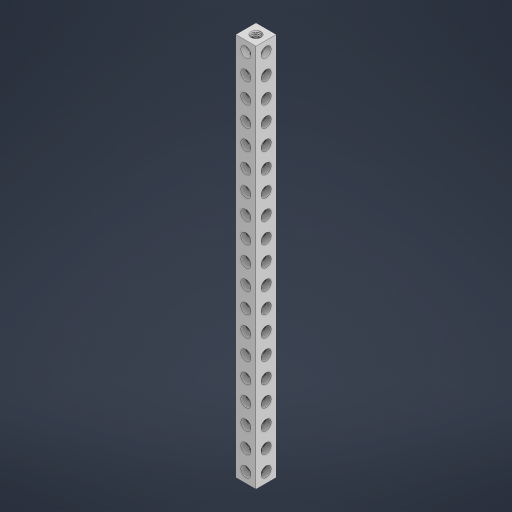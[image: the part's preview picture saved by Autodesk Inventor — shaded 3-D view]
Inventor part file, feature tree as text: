
AUTODESK INVENTOR PART (.ipt)
format: ipt  version: 2023 (Build 270158000, 158)  size: 1,242,112 bytes
history: native  units: in
note: dims shown in document units (in); Inventor stores cm internally (conversion verified against a paired STEP export)
features: mirror x1
ambient origin geometry x8: Origin, YZ Plane, XZ Plane, XY Plane, X Axis, Y Axis, Z Axis, Center Point
bodies: Solid1 (feature_tree)
feature tree (1):
  mirror  "Mirror3"
